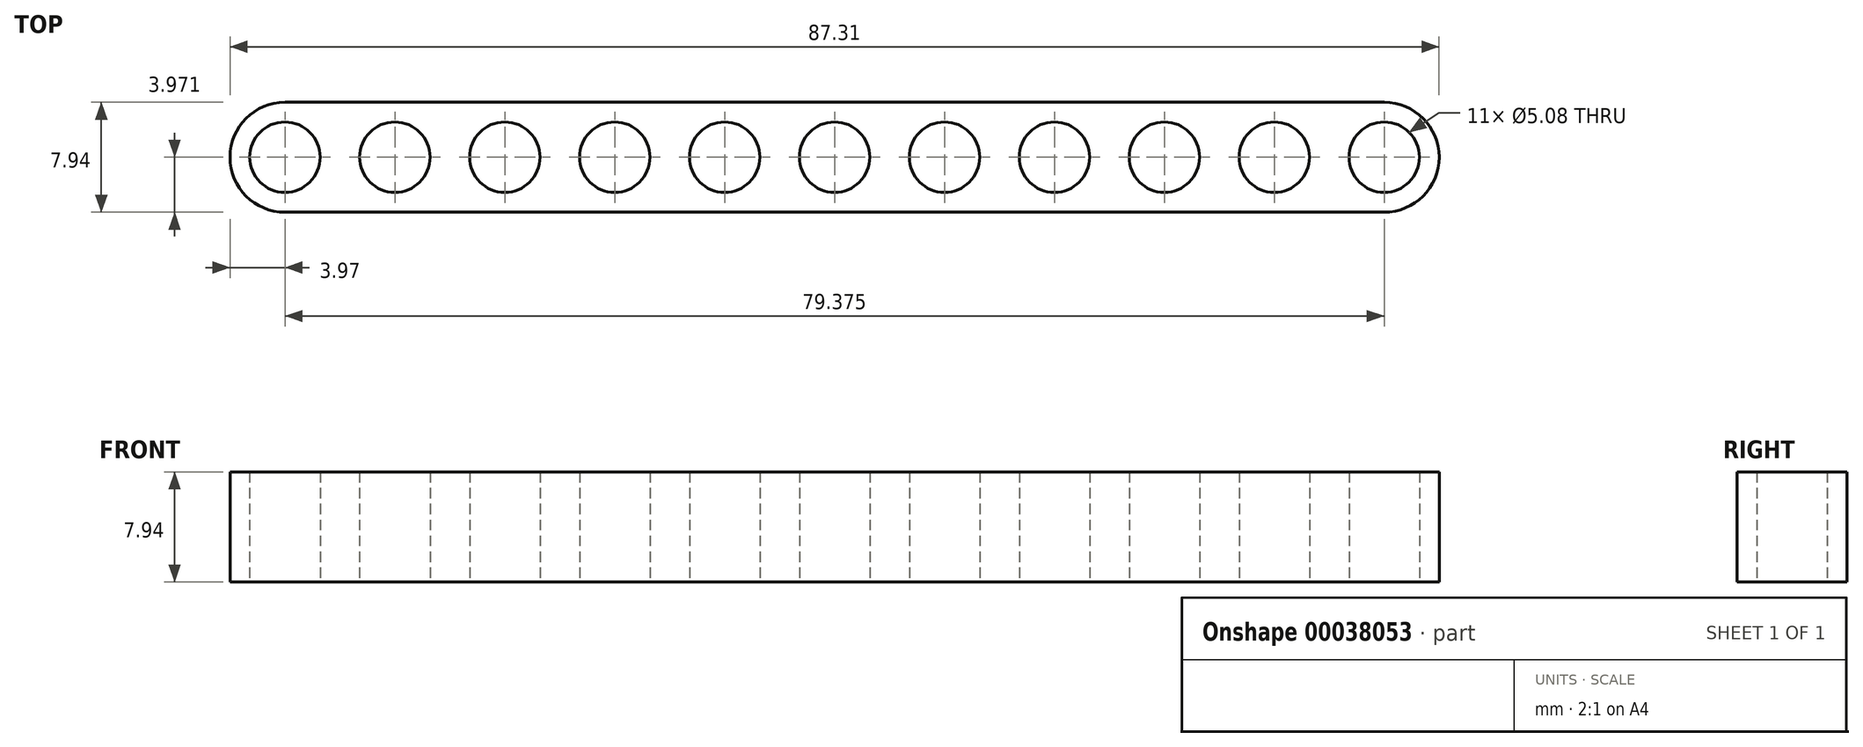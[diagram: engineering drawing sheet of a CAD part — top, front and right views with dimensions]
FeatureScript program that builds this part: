
annotation { "Feature Type Name" : "Feature", "Feature Type Description" : "" }
export const myFeature = defineFeature(function(context is Context, id is Id, definition is map)
    precondition{}
    {
        {
            var Q0;
            Q0=qCreatedBy(makeId("Top.planeOp"),FACE);
            var sketch = newSketch(context, id + "F0", { "sketchPlane" : qUnion([Q0])});
            skLineSegment(sketch, "E0.bottom", {"start": v(0, 0) * mm, "end": v(79.38, 0) * mm});
            skLineSegment(sketch, "E0.top", {"start": v(0, -7.94) * mm, "end": v(79.38, -7.94) * mm});
            skLineSegment(sketch, "E0.left", {"start": v(0, 0) * mm, "end": v(0, -7.94) * mm, "construction": true});
            skLineSegment(sketch, "E0.right", {"start": v(79.38, 0) * mm, "end": v(79.38, -7.94) * mm, "construction": true});
            skLineSegment(sketch, "E1", {"start": v(0, -3.97) * mm, "end": v(7.94, -3.97) * mm, "construction": true});
            skLineSegment(sketch, "E2", {"start": v(7.94, -3.97) * mm, "end": v(15.88, -3.97) * mm, "construction": true});
            skLineSegment(sketch, "E3", {"start": v(15.88, -3.97) * mm, "end": v(23.81, -3.97) * mm, "construction": true});
            skLineSegment(sketch, "E4", {"start": v(23.81, -3.97) * mm, "end": v(31.75, -3.97) * mm, "construction": true});
            skLineSegment(sketch, "E5", {"start": v(31.75, -3.97) * mm, "end": v(39.69, -3.97) * mm, "construction": true});
            skLineSegment(sketch, "E6", {"start": v(39.69, -3.97) * mm, "end": v(47.62, -3.97) * mm, "construction": true});
            skCircle(sketch, "E7", {"center": v(0, -3.97) * mm, "radius": 2.54 * mm});
            skCircle(sketch, "E8", {"center": v(7.94, -3.97) * mm, "radius": 2.54 * mm});
            skCircle(sketch, "E9", {"center": v(15.88, -3.97) * mm, "radius": 2.54 * mm});
            skCircle(sketch, "E10", {"center": v(23.81, -3.97) * mm, "radius": 2.54 * mm});
            skCircle(sketch, "E11", {"center": v(31.75, -3.97) * mm, "radius": 2.54 * mm});
            skCircle(sketch, "E12", {"center": v(39.69, -3.97) * mm, "radius": 2.54 * mm});
            skCircle(sketch, "E13", {"center": v(47.62, -3.97) * mm, "radius": 2.54 * mm});
            skCircle(sketch, "E14", {"center": v(79.38, -3.97) * mm, "radius": 2.54 * mm});
            skArc(sketch, "E15", {"start": v(0, 0) * mm, "mid": v(-3.97, -3.97) * mm, "end": v(0, -7.94) * mm});
            skArc(sketch, "E16", {"start": v(79.38, -7.94) * mm, "mid": v(83.34, -3.97) * mm, "end": v(79.38, 0) * mm});
            skLineSegment(sketch, "E17", {"start": v(47.62, -3.97) * mm, "end": v(55.56, -3.97) * mm, "construction": true});
            skLineSegment(sketch, "E18", {"start": v(55.56, -3.97) * mm, "end": v(63.5, -3.97) * mm, "construction": true});
            skLineSegment(sketch, "E19", {"start": v(63.5, -3.97) * mm, "end": v(71.44, -3.97) * mm, "construction": true});
            skLineSegment(sketch, "E20", {"start": v(71.44, -3.97) * mm, "end": v(79.38, -3.97) * mm, "construction": true});
            skCircle(sketch, "E21", {"center": v(55.56, -3.97) * mm, "radius": 2.54 * mm});
            skCircle(sketch, "E22", {"center": v(63.5, -3.97) * mm, "radius": 2.54 * mm});
            skCircle(sketch, "E23", {"center": v(71.44, -3.97) * mm, "radius": 2.54 * mm});
            skSolve(sketch);
        }
        {
            var Q0;
            Q0 = qSketchRegion(id + "F0", true);
            extrude(context, id + "F1", {"entities" : qUnion([Q0]), "depth" : 7.94 * mm});
        }
    });
